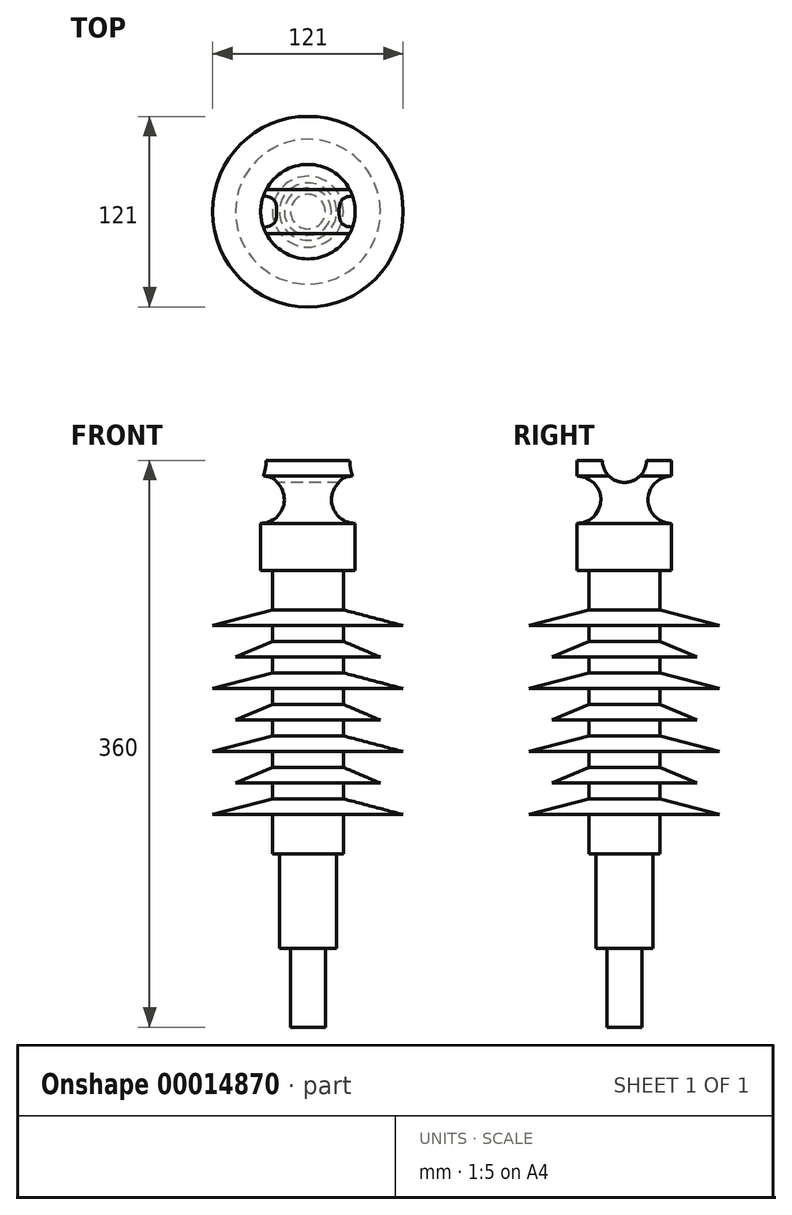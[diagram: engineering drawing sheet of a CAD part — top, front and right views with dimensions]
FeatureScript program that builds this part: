
annotation { "Feature Type Name" : "Feature", "Feature Type Description" : "" }
export const myFeature = defineFeature(function(context is Context, id is Id, definition is map)
    precondition{}
    {
        {
            var Q0;
            Q0=qCreatedBy(makeId("Front.planeOp"),FACE);
            var sketch = newSketch(context, id + "F0", { "sketchPlane" : qUnion([Q0])});
            skLineSegment(sketch, "E0", {"start": v(0, 0) * mm, "end": v(11, 0) * mm});
            skLineSegment(sketch, "E1", {"start": v(11, 0) * mm, "end": v(11, 50) * mm});
            skLineSegment(sketch, "E2", {"start": v(11, 50) * mm, "end": v(18.2, 50) * mm});
            skLineSegment(sketch, "E3", {"start": v(18.2, 50) * mm, "end": v(18.2, 110) * mm});
            skLineSegment(sketch, "E4", {"start": v(22.5, 110) * mm, "end": v(18.2, 110) * mm});
            skLineSegment(sketch, "E5", {"start": v(22.5, 110) * mm, "end": v(22.5, 110) * mm});
            skLineSegment(sketch, "E6", {"start": v(22.5, 110) * mm, "end": v(22.5, 135) * mm});
            skLineSegment(sketch, "E7", {"start": v(22.5, 290) * mm, "end": v(30, 290) * mm});
            skLineSegment(sketch, "E8", {"start": v(30, 290) * mm, "end": v(30, 320) * mm});
            skLineSegment(sketch, "E9", {"start": v(30, 350) * mm, "end": v(30, 360) * mm});
            skLineSegment(sketch, "E10", {"start": v(30, 360) * mm, "end": v(0, 360) * mm});
            skLineSegment(sketch, "E11", {"start": v(0, 360) * mm, "end": v(0, 0) * mm});
            skLineSegment(sketch, "E12", {"start": v(30, 320) * mm, "end": v(30, 315) * mm});
            skLineSegment(sketch, "E13", {"start": v(22.5, 290) * mm, "end": v(22.5, 265) * mm});
            skLineSegment(sketch, "E14", {"start": v(22.5, 265) * mm, "end": v(60.5, 255) * mm});
            skLineSegment(sketch, "E15", {"start": v(60.5, 255) * mm, "end": v(22.5, 255) * mm});
            skLineSegment(sketch, "E16", {"start": v(22.5, 255) * mm, "end": v(22.5, 245) * mm});
            skLineSegment(sketch, "E17", {"start": v(22.5, 245) * mm, "end": v(46, 235) * mm});
            skLineSegment(sketch, "E18", {"start": v(46, 235) * mm, "end": v(22.5, 235) * mm});
            skLineSegment(sketch, "E19", {"start": v(22.5, 235) * mm, "end": v(22.5, 225) * mm});
            skLineSegment(sketch, "E20", {"start": v(22.5, 225) * mm, "end": v(60.5, 215) * mm});
            skLineSegment(sketch, "E21", {"start": v(60.5, 215) * mm, "end": v(22.5, 215) * mm});
            skLineSegment(sketch, "E22", {"start": v(22.5, 215) * mm, "end": v(22.5, 205) * mm});
            skLineSegment(sketch, "E23", {"start": v(22.5, 205) * mm, "end": v(46, 195) * mm});
            skLineSegment(sketch, "E24", {"start": v(46, 195) * mm, "end": v(22.5, 195) * mm});
            skLineSegment(sketch, "E25", {"start": v(22.5, 195) * mm, "end": v(22.5, 185) * mm});
            skLineSegment(sketch, "E26", {"start": v(22.5, 185) * mm, "end": v(60.5, 175) * mm});
            skLineSegment(sketch, "E27", {"start": v(60.5, 175) * mm, "end": v(22.5, 175) * mm});
            skArc(sketch, "E28", {"start": v(30, 350) * mm, "mid": v(15, 335) * mm, "end": v(30, 320) * mm});
            skLineSegment(sketch, "E29", {"start": v(22.5, 155) * mm, "end": v(22.5, 145) * mm});
            skLineSegment(sketch, "E30", {"start": v(22.5, 145) * mm, "end": v(60.5, 135) * mm});
            skLineSegment(sketch, "E31", {"start": v(60.5, 135) * mm, "end": v(22.5, 135) * mm});
            skPoint(sketch, "E32.start.orphan", {"position": v(22.5, 165) * mm});
            skLineSegment(sketch, "E33", {"start": v(22.5, 165) * mm, "end": v(46, 155) * mm});
            skLineSegment(sketch, "E34", {"start": v(46, 155) * mm, "end": v(22.5, 155) * mm});
            skLineSegment(sketch, "E35.trimOffspring", {"start": v(22.5, 265) * mm, "end": v(22.5, 290) * mm});
            skLineSegment(sketch, "E36.trimOffspring", {"start": v(22.5, 245) * mm, "end": v(22.5, 255) * mm});
            skLineSegment(sketch, "E37.trimOffspring", {"start": v(22.5, 225) * mm, "end": v(22.5, 235) * mm});
            skLineSegment(sketch, "E38.trimOffspring", {"start": v(22.5, 205) * mm, "end": v(22.5, 215) * mm});
            skLineSegment(sketch, "E39.trimOffspring", {"start": v(22.5, 185) * mm, "end": v(22.5, 195) * mm});
            skLineSegment(sketch, "E40.trimOffspring", {"start": v(22.5, 165) * mm, "end": v(22.5, 175) * mm});
            skLineSegment(sketch, "E41.trimOffspring", {"start": v(22.5, 145) * mm, "end": v(22.5, 155) * mm});
            skSolve(sketch);
        }
        {
            var Q0;
            Q0=makeQuery(id+"F0.imprint","IMPRINT",FACE,{"disambiguationData":[TD([[makeQuery(id+"F0.imprint","IMPRINT",EDGE,{"derivedFrom":sQuery(id+"F0.wireOp",EDGE,"E0")}),1.0]])]});
            var Q1;
            Q1=sQuery(id+"F0.wireOp",EDGE,"E8");
            var Q2;
            Q2=sQuery(id+"F0.wireOp",EDGE,"E28");
            var Q3;
            Q3=sQuery(id+"F0.wireOp",EDGE,"E10");
            var Q4;
            Q4=sQuery(id+"F0.wireOp",EDGE,"E14");
            var Q5;
            Q5=sQuery(id+"F0.wireOp",EDGE,"E13");
            var Q6;
            Q6=sQuery(id+"F0.wireOp",EDGE,"E15");
            var Q7;
            Q7=sQuery(id+"F0.wireOp",EDGE,"E16");
            var Q8;
            Q8=sQuery(id+"F0.wireOp",EDGE,"E17");
            var Q9;
            Q9=sQuery(id+"F0.wireOp",EDGE,"E18");
            var Q10;
            Q10=sQuery(id+"F0.wireOp",EDGE,"E37.trimOffspring");
            var Q11;
            Q11=sQuery(id+"F0.wireOp",EDGE,"E20");
            var Q12;
            Q12=sQuery(id+"F0.wireOp",EDGE,"E21");
            var Q13;
            Q13=sQuery(id+"F0.wireOp",EDGE,"E38.trimOffspring");
            var Q14;
            Q14=sQuery(id+"F0.wireOp",EDGE,"E23");
            var Q15;
            Q15=sQuery(id+"F0.wireOp",EDGE,"E24");
            var Q16;
            Q16=sQuery(id+"F0.wireOp",EDGE,"E25");
            var Q17;
            Q17=sQuery(id+"F0.wireOp",EDGE,"E26");
            var Q18;
            Q18=sQuery(id+"F0.wireOp",EDGE,"E27");
            var Q19;
            Q19=sQuery(id+"F0.wireOp",EDGE,"E40.trimOffspring");
            var Q20;
            Q20=sQuery(id+"F0.wireOp",EDGE,"E33");
            var Q21;
            Q21=sQuery(id+"F0.wireOp",EDGE,"E34");
            var Q22;
            Q22=sQuery(id+"F0.wireOp",EDGE,"E41.trimOffspring");
            var Q23;
            Q23=sQuery(id+"F0.wireOp",EDGE,"E40.trimOffspring");
            var Q24;
            Q24=sQuery(id+"F0.wireOp",EDGE,"E30");
            var Q25;
            Q25=sQuery(id+"F0.wireOp",EDGE,"E31");
            var Q26;
            Q26=sQuery(id+"F0.wireOp",EDGE,"E9");
            var Q27;
            Q27=sQuery(id+"F0.wireOp",EDGE,"E6");
            var Q28;
            Q28=sQuery(id+"F0.wireOp",EDGE,"E4");
            var Q29;
            Q29=sQuery(id+"F0.wireOp",EDGE,"E3");
            var Q30;
            Q30=sQuery(id+"F0.wireOp",EDGE,"E2");
            var Q31;
            Q31=sQuery(id+"F0.wireOp",EDGE,"E1");
            var Q32;
            Q32=sQuery(id+"F0.wireOp",EDGE,"E0");
            var Q33;
            Q33=sQuery(id+"F0.wireOp",EDGE,"E7");
            var Q34;
            Q34=sQuery(id+"F0.wireOp",EDGE,"E11");
            revolve(context, id + "F1", {"entities" : qUnion([Q0]), "surfaceEntities" : qUnion([Q1, Q2, Q3, Q4, Q5, Q6, Q7, Q8, Q9, Q10, Q11, Q12, Q13, Q14, Q15, Q16, Q17, Q18, Q19, Q20, Q21, Q22, Q23, Q24, Q25, Q26, Q27, Q28, Q29, Q30, Q31, Q32, Q33]), "axis" : qUnion([Q34]), "revolveType" : RevolveType.FULL});
        }
        {
            var Q0;
            Q0=qCreatedBy(makeId("Right.planeOp"),FACE);
            var sketch = newSketch(context, id + "F2", { "sketchPlane" : qUnion([Q0])});
            skCircle(sketch, "E42", {"center": v(0, 360) * mm, "radius": 14 * mm});
            skSolve(sketch);
        }
        {
            var Q0;
            Q0 = qSketchRegion(id + "F2", true);
            extrude(context, id + "F3", {"entities" : qUnion([Q0]), "operationType" : NewBodyOperationType.REMOVE, "depth" : 30 * mm, "hasSecondDirection" : true, "secondDirectionOppositeDirection" : true, "secondDirectionDepth" : 30 * mm});
        }
    });
